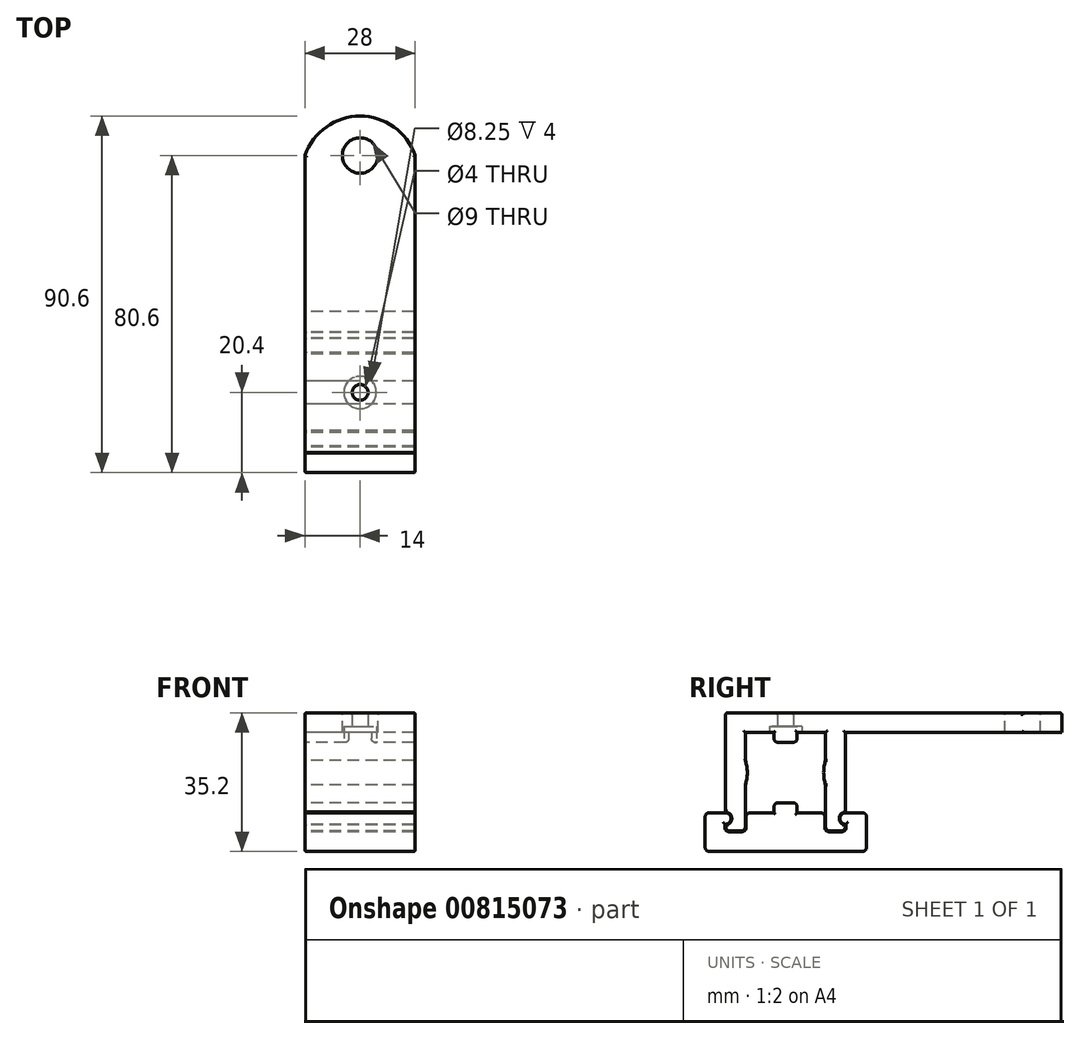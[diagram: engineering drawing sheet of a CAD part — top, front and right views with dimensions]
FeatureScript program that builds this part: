
annotation { "Feature Type Name" : "Feature", "Feature Type Description" : "" }
export const myFeature = defineFeature(function(context is Context, id is Id, definition is map)
    precondition{}
    {
        {
            var Q0;
            Q0=qCreatedBy(makeId("Right.planeOp"),FACE);
            var sketch = newSketch(context, id + "F0", { "sketchPlane" : qUnion([Q0])});
            skLineSegment(sketch, "E0.bottom", {"start": v(10, -10) * mm, "end": v(-10, -10) * mm, "construction": true});
            skLineSegment(sketch, "E0.top", {"start": v(10, 10) * mm, "end": v(-10, 10) * mm, "construction": true});
            skLineSegment(sketch, "E0.left", {"start": v(10, -10) * mm, "end": v(10, 10) * mm, "construction": true});
            skLineSegment(sketch, "E0.right", {"start": v(-10, -10) * mm, "end": v(-10, 10) * mm, "construction": true});
            skPoint(sketch, "E0.middle", {"position": v(0, 0) * mm});
            skLineSegment(sketch, "E1.bottom", {"start": v(-4, 4) * mm, "end": v(4, 4) * mm, "construction": true});
            skLineSegment(sketch, "E1.top", {"start": v(-4, -4) * mm, "end": v(4, -4) * mm, "construction": true});
            skLineSegment(sketch, "E1.left", {"start": v(-4, 4) * mm, "end": v(-4, -4) * mm, "construction": true});
            skLineSegment(sketch, "E1.right", {"start": v(4, 4) * mm, "end": v(4, -4) * mm, "construction": true});
            skLineSegment(sketch, "E2.bottom", {"start": v(3.15, -25) * mm, "end": v(-3.15, -25) * mm, "construction": true});
            skLineSegment(sketch, "E2.top", {"start": v(3.15, 25) * mm, "end": v(-3.15, 25) * mm, "construction": true});
            skLineSegment(sketch, "E2.left", {"start": v(3.15, -25) * mm, "end": v(3.15, 25) * mm, "construction": true});
            skLineSegment(sketch, "E2.right", {"start": v(-3.15, -25) * mm, "end": v(-3.15, 25) * mm, "construction": true});
            skLineSegment(sketch, "E3.bottom", {"start": v(25, -3.15) * mm, "end": v(-25, -3.15) * mm, "construction": true});
            skLineSegment(sketch, "E3.top", {"start": v(25, 3.15) * mm, "end": v(-25, 3.15) * mm, "construction": true});
            skLineSegment(sketch, "E3.left", {"start": v(25, -3.15) * mm, "end": v(25, 3.15) * mm, "construction": true});
            skLineSegment(sketch, "E3.right", {"start": v(-25, -3.15) * mm, "end": v(-25, 3.15) * mm, "construction": true});
            skSolve(sketch);
        }
        {
            assignVariable(context, id + "F1", {"name" : "ArmW", "anyValue" : 28});
        }
        {
            assignVariable(context, id + "F2", {"name" : "NobH", "anyValue" : 2.5});
        }
        {
            var Q0;
            Q0=qCreatedBy(makeId("Right.planeOp"),FACE);
            var sketch = newSketch(context, id + "F3", { "sketchPlane" : qUnion([Q0])});
            skLineSegment(sketch, "E4.bottom", {"start": v(-2.95, 10.2) * mm, "end": v(2.95, 10.2) * mm});
            skLineSegment(sketch, "E4.top", {"start": v(-1.95, 7.7) * mm, "end": v(1.95, 7.7) * mm});
            skLineSegment(sketch, "E4.left", {"start": v(-2.95, 10.2) * mm, "end": v(-2.95, 8.7) * mm});
            skLineSegment(sketch, "E4.right", {"start": v(2.95, 10.2) * mm, "end": v(2.95, 8.7) * mm});
            skLineSegment(sketch, "E5.bottom", {"start": v(-15.2, 15.2) * mm, "end": v(70.2, 15.2) * mm});
            skLineSegment(sketch, "E5.top", {"start": v(-15.2, 10.2) * mm, "end": v(15.2, 10.2) * mm});
            skLineSegment(sketch, "E5.left", {"start": v(-15.2, 15.2) * mm, "end": v(-15.2, 10.2) * mm});
            skLineSegment(sketch, "E5.right", {"start": v(70.2, 15.2) * mm, "end": v(70.2, 10.2) * mm});
            skLineSegment(sketch, "E6.bottom", {"start": v(10.2, 10.2) * mm, "end": v(15.2, 10.2) * mm});
            skLineSegment(sketch, "E6.top", {"start": v(11.2, -14.8) * mm, "end": v(14.2, -14.8) * mm});
            skLineSegment(sketch, "E6.left", {"start": v(10.2, 10.2) * mm, "end": v(10.2, -13.8) * mm});
            skLineSegment(sketch, "E6.right", {"start": v(15.2, -10) * mm, "end": v(15.2, -10.09) * mm});
            skLineSegment(sketch, "E7.bottom", {"start": v(-15.2, 10.2) * mm, "end": v(-10.2, 10.2) * mm});
            skLineSegment(sketch, "E7.top", {"start": v(-14.2, -14.8) * mm, "end": v(-11.2, -14.8) * mm});
            skLineSegment(sketch, "E7.left", {"start": v(-15.2, 10.2) * mm, "end": v(-15.2, -10) * mm});
            skLineSegment(sketch, "E7.right", {"start": v(-10.2, 10.2) * mm, "end": v(-10.2, -13.8) * mm});
            skLineSegment(sketch, "E8.bottom", {"start": v(9.7, -1.7) * mm, "end": v(-9.7, -1.7) * mm, "construction": true});
            skLineSegment(sketch, "E8.top", {"start": v(9.7, 1.7) * mm, "end": v(-9.7, 1.7) * mm, "construction": true});
            skLineSegment(sketch, "E8.left", {"start": v(9.7, -1.7) * mm, "end": v(9.7, 1.7) * mm, "construction": true});
            skLineSegment(sketch, "E8.right", {"start": v(-9.7, -1.7) * mm, "end": v(-9.7, 1.7) * mm, "construction": true});
            skPoint(sketch, "E8.middle", {"position": v(0, 0) * mm});
            skPoint(sketch, "E9", {"position": v(-10.2, 3.15) * mm});
            skPoint(sketch, "E10", {"position": v(-10.2, -3.15) * mm});
            skPoint(sketch, "E11", {"position": v(-9.7, 0) * mm});
            skPoint(sketch, "E12", {"position": v(10.2, 3.15) * mm});
            skPoint(sketch, "E13", {"position": v(10.2, -3.15) * mm});
            skPoint(sketch, "E14", {"position": v(9.7, 0) * mm});
            skArc(sketch, "E15", {"start": v(-10.2, -3.15) * mm, "mid": v(-9.7, 0) * mm, "end": v(-10.2, 3.15) * mm});
            skArc(sketch, "E16", {"start": v(10.2, 3.15) * mm, "mid": v(9.7, 0) * mm, "end": v(10.2, -3.15) * mm});
            skLineSegment(sketch, "E17.bottom", {"start": v(-9, -10.2) * mm, "end": v(9, -10.2) * mm});
            skLineSegment(sketch, "E17.left", {"start": v(-10, -11.2) * mm, "end": v(-10, -14) * mm});
            skLineSegment(sketch, "E17.right", {"start": v(10, -11.2) * mm, "end": v(10, -14) * mm});
            skLineSegment(sketch, "E18.bottom", {"start": v(-19.4, -10.2) * mm, "end": v(-15.4, -10.2) * mm});
            skLineSegment(sketch, "E18.top", {"start": v(-19.4, -20) * mm, "end": v(-15.4, -20) * mm});
            skLineSegment(sketch, "E18.left", {"start": v(-20.4, -11.2) * mm, "end": v(-20.4, -19) * mm});
            skLineSegment(sketch, "E18.right", {"start": v(-15.4, -13.1) * mm, "end": v(-15.4, -14) * mm});
            skLineSegment(sketch, "E19.bottom", {"start": v(15.4, -10.2) * mm, "end": v(19.6, -10.2) * mm});
            skLineSegment(sketch, "E19.top", {"start": v(15.6, -20) * mm, "end": v(19.6, -20) * mm});
            skLineSegment(sketch, "E19.left", {"start": v(15.4, -13.1) * mm, "end": v(15.4, -14) * mm});
            skLineSegment(sketch, "E19.right", {"start": v(20.6, -11.2) * mm, "end": v(20.6, -19) * mm});
            skLineSegment(sketch, "E20.bottom", {"start": v(-14.4, -15) * mm, "end": v(-11, -15) * mm});
            skLineSegment(sketch, "E20.top", {"start": v(-15.4, -20) * mm, "end": v(15.6, -20) * mm});
            skLineSegment(sketch, "E20.left", {"start": v(-15.4, -15) * mm, "end": v(-15.4, -20) * mm});
            skLineSegment(sketch, "E20.right", {"start": v(15.6, -20) * mm, "end": v(15.6, -20) * mm});
            skLineSegment(sketch, "E21.bottom", {"start": v(-1.95, -7.7) * mm, "end": v(1.95, -7.7) * mm});
            skLineSegment(sketch, "E21.top", {"start": v(-2.95, -10.2) * mm, "end": v(2.95, -10.2) * mm});
            skLineSegment(sketch, "E21.left", {"start": v(-2.95, -8.7) * mm, "end": v(-2.95, -10.2) * mm});
            skLineSegment(sketch, "E21.right", {"start": v(2.95, -8.7) * mm, "end": v(2.95, -10.2) * mm});
            skPoint(sketch, "E22", {"position": v(-15.2, -10) * mm});
            skPoint(sketch, "E23", {"position": v(-15.2, -13.3) * mm});
            skPoint(sketch, "E24", {"position": v(-15.4, -13.1) * mm});
            skPoint(sketch, "E25", {"position": v(-13.65, -11.8) * mm});
            skPoint(sketch, "E26", {"position": v(-13.85, -11.8) * mm});
            skArc(sketch, "E27", {"start": v(-15.2, -13.3) * mm, "mid": v(-13.64, -11.65) * mm, "end": v(-15.2, -10) * mm});
            skArc(sketch, "E28", {"start": v(-15.4, -13.1) * mm, "mid": v(-13.84, -11.65) * mm, "end": v(-15.4, -10.2) * mm});
            skLineSegment(sketch, "E29.trimOffspring", {"start": v(-15.2, -13.3) * mm, "end": v(-15.2, -13.8) * mm});
            skPoint(sketch, "E30.MirrorP", {"position": v(15.2, -10) * mm});
            skArc(sketch, "E31.MirrorCS", {"start": v(15.2, -13.3) * mm, "mid": v(13.64, -11.65) * mm, "end": v(15.2, -10) * mm});
            skArc(sketch, "E32.MirrorCS", {"start": v(15.4, -13.1) * mm, "mid": v(13.84, -11.65) * mm, "end": v(15.4, -10.2) * mm});
            skPoint(sketch, "E33.MirrorP", {"position": v(13.85, -11.8) * mm});
            skPoint(sketch, "E34.MirrorP", {"position": v(13.65, -11.8) * mm});
            skPoint(sketch, "E35.MirrorP", {"position": v(15.4, -13.1) * mm});
            skPoint(sketch, "E36.MirrorP", {"position": v(15.2, -13.3) * mm});
            skLineSegment(sketch, "E37.trimOffspring", {"start": v(15.2, -13.3) * mm, "end": v(15.2, -13.8) * mm});
            skPoint(sketch, "E38.visualSharp", {"position": v(-15.2, 15.2) * mm});
            skPoint(sketch, "E39.visualSharp", {"position": v(-20.4, -10.2) * mm});
            skArc(sketch, "E39.filletArc", {"start": v(-19.4, -10.2) * mm, "mid": v(-20.1, -10.5) * mm, "end": v(-20.4, -11.2) * mm});
            skPoint(sketch, "E40.visualSharp", {"position": v(-20.4, -20) * mm});
            skArc(sketch, "E40.filletArc", {"start": v(-20.4, -19) * mm, "mid": v(-20.1, -19.7) * mm, "end": v(-19.4, -20) * mm});
            skPoint(sketch, "E41.visualSharp", {"position": v(20.6, -20) * mm});
            skArc(sketch, "E41.filletArc", {"start": v(19.6, -20) * mm, "mid": v(20.3, -19.7) * mm, "end": v(20.6, -19) * mm});
            skPoint(sketch, "E42.visualSharp", {"position": v(20.6, -10.2) * mm});
            skArc(sketch, "E42.filletArc", {"start": v(20.6, -11.2) * mm, "mid": v(20.3, -10.5) * mm, "end": v(19.6, -10.2) * mm});
            skPoint(sketch, "E43.visualSharp", {"position": v(-2.95, -7.7) * mm});
            skArc(sketch, "E43.filletArc", {"start": v(-1.95, -7.7) * mm, "mid": v(-2.66, -8) * mm, "end": v(-2.95, -8.7) * mm});
            skPoint(sketch, "E44.visualSharp", {"position": v(2.95, -7.7) * mm});
            skArc(sketch, "E44.filletArc", {"start": v(2.95, -8.7) * mm, "mid": v(2.66, -8) * mm, "end": v(1.95, -7.7) * mm});
            skPoint(sketch, "E45.visualSharp", {"position": v(-2.95, 7.7) * mm});
            skArc(sketch, "E45.filletArc", {"start": v(-2.95, 8.7) * mm, "mid": v(-2.66, 8) * mm, "end": v(-1.95, 7.7) * mm});
            skPoint(sketch, "E46.visualSharp", {"position": v(2.95, 7.7) * mm});
            skArc(sketch, "E46.filletArc", {"start": v(1.95, 7.7) * mm, "mid": v(2.66, 8) * mm, "end": v(2.95, 8.7) * mm});
            skPoint(sketch, "E47.visualSharp", {"position": v(10.2, -14.8) * mm});
            skArc(sketch, "E47.filletArc", {"start": v(10.2, -13.8) * mm, "mid": v(10.5, -14.5) * mm, "end": v(11.2, -14.8) * mm});
            skPoint(sketch, "E48.visualSharp", {"position": v(15.2, -14.8) * mm});
            skArc(sketch, "E48.filletArc", {"start": v(14.2, -14.8) * mm, "mid": v(14.9, -14.5) * mm, "end": v(15.2, -13.8) * mm});
            skPoint(sketch, "E49.visualSharp", {"position": v(-10, -10.2) * mm});
            skArc(sketch, "E49.filletArc", {"start": v(-9, -10.2) * mm, "mid": v(-9.7, -10.5) * mm, "end": v(-10, -11.2) * mm});
            skPoint(sketch, "E50.visualSharp", {"position": v(10, -10.2) * mm});
            skArc(sketch, "E50.filletArc", {"start": v(10, -11.2) * mm, "mid": v(9.7, -10.5) * mm, "end": v(9, -10.2) * mm});
            skPoint(sketch, "E51.visualSharp", {"position": v(-10.2, -14.8) * mm});
            skArc(sketch, "E51.filletArc", {"start": v(-11.2, -14.8) * mm, "mid": v(-10.5, -14.5) * mm, "end": v(-10.2, -13.8) * mm});
            skPoint(sketch, "E52.visualSharp", {"position": v(-15.2, -14.8) * mm});
            skArc(sketch, "E52.filletArc", {"start": v(-15.2, -13.8) * mm, "mid": v(-14.9, -14.5) * mm, "end": v(-14.2, -14.8) * mm});
            skArc(sketch, "E53.filletArc", {"start": v(-15.4, -14) * mm, "mid": v(-15.1, -14.7) * mm, "end": v(-14.4, -15) * mm});
            skArc(sketch, "E54.filletArc", {"start": v(14.4, -15) * mm, "mid": v(15.1, -14.7) * mm, "end": v(15.4, -14) * mm});
            skLineSegment(sketch, "E55.trimOffspring", {"start": v(11, -15) * mm, "end": v(14.4, -15) * mm});
            skPoint(sketch, "E56.visualSharp", {"position": v(-10, -15) * mm});
            skArc(sketch, "E56.filletArc", {"start": v(-11, -15) * mm, "mid": v(-10.3, -14.7) * mm, "end": v(-10, -14) * mm});
            skPoint(sketch, "E57.visualSharp", {"position": v(10, -15) * mm});
            skArc(sketch, "E57.filletArc", {"start": v(10, -14) * mm, "mid": v(10.3, -14.7) * mm, "end": v(11, -15) * mm});
            skPoint(sketch, "E58.visualSharp", {"position": v(-15.4, -10.2) * mm});
            skLineSegment(sketch, "E59", {"start": v(15.2, 10.2) * mm, "end": v(15.2, -10.09) * mm});
            skLineSegment(sketch, "E60", {"start": v(15.2, 10.2) * mm, "end": v(70.2, 10.2) * mm});
            skSolve(sketch);
        }
        {
            var Q0;
            Q0=qSketchRegion(id+"F3",true);
            extrude(context, id + "F4", {"entities" : qUnion([Q0]), "depth" : (getVariable(context, 'ArmW')) * mm, "offsetDistance" : 25 * mm});
        }
        {
            var Q0;
            Q0=makeQuery(id+"F4.opExtrude","SWEPT_FACE",FACE,{"disambiguationData":[OSD([sQuery(id+"F3.wireOp",EDGE,"E4.top")])]});
            cPlane(context, id + "F5", {"entities" : qUnion([Q0]), "cplaneType" : CPlaneType.OFFSET, "offset" : 0 * mm, "width" : 150 * mm, "height" : 150 * mm});
        }
        {
            var Q0;
            Q0=qCreatedBy(id+"F5.planeOp",FACE);
            var sketch = newSketch(context, id + "F6", { "sketchPlane" : qUnion([Q0])});
            skLineSegment(sketch, "E61", {"start": v(28, -15.2) * mm, "end": v(0, 15.2) * mm, "construction": true});
            skLineSegment(sketch, "E62", {"start": v(28, 15.2) * mm, "end": v(0, -15.2) * mm, "construction": true});
            skPoint(sketch, "E63", {"position": v(14, 0) * mm});
            skPoint(sketch, "E64.0", {"position": v(28, -15.2) * mm});
            skLineSegment(sketch, "E65.bottom", {"start": v(0, -15.2) * mm, "end": v(2, -15.2) * mm, "construction": true});
            skLineSegment(sketch, "E65.top", {"start": v(0, -13.2) * mm, "end": v(2, -13.2) * mm, "construction": true});
            skLineSegment(sketch, "E65.left", {"start": v(0, -15.2) * mm, "end": v(0, -13.2) * mm, "construction": true});
            skLineSegment(sketch, "E65.right", {"start": v(2, -15.2) * mm, "end": v(2, -13.2) * mm, "construction": true});
            skLineSegment(sketch, "E66.bottom", {"start": v(26, -13.2) * mm, "end": v(28, -13.2) * mm, "construction": true});
            skLineSegment(sketch, "E66.top", {"start": v(26, -15.2) * mm, "end": v(28, -15.2) * mm, "construction": true});
            skLineSegment(sketch, "E66.left", {"start": v(26, -13.2) * mm, "end": v(26, -15.2) * mm, "construction": true});
            skLineSegment(sketch, "E66.right", {"start": v(28, -13.2) * mm, "end": v(28, -15.2) * mm, "construction": true});
            skLineSegment(sketch, "E67.bottom", {"start": v(26, 15.2) * mm, "end": v(28, 15.2) * mm, "construction": true});
            skLineSegment(sketch, "E67.top", {"start": v(26, 13.2) * mm, "end": v(28, 13.2) * mm, "construction": true});
            skLineSegment(sketch, "E67.left", {"start": v(26, 15.2) * mm, "end": v(26, 13.2) * mm, "construction": true});
            skLineSegment(sketch, "E67.right", {"start": v(28, 15.2) * mm, "end": v(28, 13.2) * mm, "construction": true});
            skLineSegment(sketch, "E68.bottom", {"start": v(0, 15.2) * mm, "end": v(2, 15.2) * mm, "construction": true});
            skLineSegment(sketch, "E68.top", {"start": v(0, 13.2) * mm, "end": v(2, 13.2) * mm, "construction": true});
            skLineSegment(sketch, "E68.left", {"start": v(0, 15.2) * mm, "end": v(0, 13.2) * mm, "construction": true});
            skLineSegment(sketch, "E68.right", {"start": v(2, 15.2) * mm, "end": v(2, 13.2) * mm, "construction": true});
            skSolve(sketch);
        }
        {
            var Q0;
            Q0=sQuery(id+"F6.wireOp",VERTEX,"E63");
            var Q1;
            Q1=makeQuery(id+"F4.opExtrude","SWEPT_BODY",BODY,{"disambiguationData":[OSD([sQuery(id+"F3.wireOp",EDGE,"E4.top"),sQuery(id+"F3.wireOp",EDGE,"E4.left"),sQuery(id+"F3.wireOp",EDGE,"E4.right"),sQuery(id+"F3.wireOp",EDGE,"E5.bottom"),sQuery(id+"F3.wireOp",EDGE,"E5.top"),sQuery(id+"F3.wireOp",EDGE,"E5.left"),sQuery(id+"F3.wireOp",EDGE,"E5.right"),sQuery(id+"F3.wireOp",EDGE,"E6.top"),sQuery(id+"F3.wireOp",EDGE,"E6.left"),sQuery(id+"F3.wireOp",EDGE,"E6.right"),sQuery(id+"F3.wireOp",EDGE,"E7.top"),sQuery(id+"F3.wireOp",EDGE,"E7.left"),sQuery(id+"F3.wireOp",EDGE,"E7.right"),sQuery(id+"F3.wireOp",EDGE,"E15"),sQuery(id+"F3.wireOp",EDGE,"E16"),sQuery(id+"F3.wireOp",EDGE,"E27"),sQuery(id+"F3.wireOp",EDGE,"E29.trimOffspring"),sQuery(id+"F3.wireOp",EDGE,"E31.MirrorCS"),sQuery(id+"F3.wireOp",EDGE,"E37.trimOffspring"),sQuery(id+"F3.wireOp",EDGE,"E45.filletArc"),sQuery(id+"F3.wireOp",EDGE,"E46.filletArc"),sQuery(id+"F3.wireOp",EDGE,"E47.filletArc"),sQuery(id+"F3.wireOp",EDGE,"E48.filletArc"),sQuery(id+"F3.wireOp",EDGE,"E51.filletArc"),sQuery(id+"F3.wireOp",EDGE,"E52.filletArc"),sQuery(id+"F3.wireOp",EDGE,"E59")])]});
            hole(context, id + "F7", {"style" : HoleStyle.C_BORE, "endStyle" : HoleEndStyle.THROUGH, "holeDiameter" : 4 * mm, "cBoreDiameter" : 8.25 * mm, "cBoreDepth" : (getVariable(context, 'NobH') + 1.5) * mm, "majorDiameter" : 3 * mm, "isTappedThrough" : true, "tappedDepth" : 6.5 * mm, "tapClearance" : 3, "startFromSketch" : true, "locations" : qUnion([Q0]), "scope" : qUnion([Q1])});
        }
        {
            var Q0;
            Q0=makeQuery(id+"F4.opExtrude","SWEPT_FACE",FACE,{"disambiguationData":[OSD([sQuery(id+"F3.wireOp",EDGE,"E5.bottom")])]});
            var sketch = newSketch(context, id + "F8", { "sketchPlane" : qUnion([Q0])});
            skPoint(sketch, "E69.0", {"position": v(28, 15.2) * mm});
            skPoint(sketch, "E70.0", {"position": v(0, 15.2) * mm});
            skLineSegment(sketch, "E71.bottom", {"start": v(0, 15.2) * mm, "end": v(28, 15.2) * mm, "construction": true});
            skLineSegment(sketch, "E71.top", {"start": v(0, 60.2) * mm, "end": v(28, 60.2) * mm, "construction": true});
            skLineSegment(sketch, "E71.left", {"start": v(0, 15.2) * mm, "end": v(0, 60.2) * mm, "construction": true});
            skLineSegment(sketch, "E71.right", {"start": v(28, 15.2) * mm, "end": v(28, 60.2) * mm, "construction": true});
            skPoint(sketch, "E72", {"position": v(14, 60.2) * mm});
            skArc(sketch, "E73", {"start": v(28, 60.2) * mm, "mid": v(14, 70.2) * mm, "end": v(0, 60.2) * mm});
            skSolve(sketch);
        }
        {
            var Q0;
            Q0=sQuery(id+"F8.wireOp",VERTEX,"E72");
            var Q1;
            Q1=makeQuery(id+"F4.opExtrude","SWEPT_BODY",BODY,{"disambiguationData":[OSD([sQuery(id+"F3.wireOp",EDGE,"E4.top"),sQuery(id+"F3.wireOp",EDGE,"E4.left"),sQuery(id+"F3.wireOp",EDGE,"E4.right"),sQuery(id+"F3.wireOp",EDGE,"E5.bottom"),sQuery(id+"F3.wireOp",EDGE,"E5.top"),sQuery(id+"F3.wireOp",EDGE,"E5.left"),sQuery(id+"F3.wireOp",EDGE,"E5.right"),sQuery(id+"F3.wireOp",EDGE,"E6.top"),sQuery(id+"F3.wireOp",EDGE,"E6.left"),sQuery(id+"F3.wireOp",EDGE,"E7.top"),sQuery(id+"F3.wireOp",EDGE,"E7.left"),sQuery(id+"F3.wireOp",EDGE,"E7.right"),sQuery(id+"F3.wireOp",EDGE,"E15"),sQuery(id+"F3.wireOp",EDGE,"E16"),sQuery(id+"F3.wireOp",EDGE,"E27"),sQuery(id+"F3.wireOp",EDGE,"E29.trimOffspring"),sQuery(id+"F3.wireOp",EDGE,"E31.MirrorCS"),sQuery(id+"F3.wireOp",EDGE,"E37.trimOffspring"),sQuery(id+"F3.wireOp",EDGE,"E45.filletArc"),sQuery(id+"F3.wireOp",EDGE,"E46.filletArc"),sQuery(id+"F3.wireOp",EDGE,"E47.filletArc"),sQuery(id+"F3.wireOp",EDGE,"E48.filletArc"),sQuery(id+"F3.wireOp",EDGE,"E51.filletArc"),sQuery(id+"F3.wireOp",EDGE,"E52.filletArc"),sQuery(id+"F3.wireOp",EDGE,"E59"),sQuery(id+"F3.wireOp",EDGE,"E60")])]});
            hole(context, id + "F9", {"style" : HoleStyle.SIMPLE, "endStyle" : HoleEndStyle.THROUGH, "holeDiameter" : 9 * mm, "majorDiameter" : 5 * mm, "isTappedThrough" : true, "tappedDepth" : 6.5 * mm, "tapClearance" : 3, "startFromSketch" : true, "locations" : qUnion([Q0]), "scope" : qUnion([Q1])});
        }
        {
            var Q0;
            {var subQ0=sQuery(id+"F8.wireOp",EDGE,"E73");var subQ1=sQuery(id+"F3.wireOp",EDGE,"E5.bottom");var subQ2=makeQuery(id+"F4.opExtrude","SWEPT_FACE",FACE,{"disambiguationData":[OSD([subQ1])]});var subQ3=makeQuery(id+"F11.opFillet","BLEND_EDGE",EDGE,{"blendedFrom":[makeQuery(id+"F4.opExtrude","CAP_EDGE",EDGE,{"disambiguationData":[OSD([subQ1])],"isStart":true}),subQ2],"blendedInto":[subQ2]});var subQ4=makeQuery(id+"F8.imprint","INTERSECT",VERTEX,{"derivedFrom":[subQ3,subQ0]});Q0=makeQuery(id+"F8.imprint","IMPRINT",FACE,{"disambiguationData":[TD([[makeQuery(id+"F8.imprint","IMPRINT",EDGE,{"disambiguationData":[TD([[subQ4,1.0]])],"derivedFrom":subQ0}),-1.0]])]});}
            var Q1;
            {var subQ0=sQuery(id+"F8.wireOp",EDGE,"E73");var subQ1=sQuery(id+"F3.wireOp",EDGE,"E5.bottom");var subQ2=makeQuery(id+"F4.opExtrude","SWEPT_FACE",FACE,{"disambiguationData":[OSD([subQ1])]});var subQ3=makeQuery(id+"F11.opFillet","BLEND_EDGE",EDGE,{"blendedFrom":[makeQuery(id+"F4.opExtrude","CAP_EDGE",EDGE,{"disambiguationData":[OSD([subQ1])],"isStart":false}),subQ2],"blendedInto":[subQ2]});var subQ4=makeQuery(id+"F8.imprint","INTERSECT",VERTEX,{"derivedFrom":[subQ3,subQ0]});Q1=makeQuery(id+"F8.imprint","IMPRINT",FACE,{"disambiguationData":[TD([[makeQuery(id+"F8.imprint","IMPRINT",EDGE,{"disambiguationData":[TD([[subQ4,-1.0]])],"derivedFrom":subQ0}),-1.0]])]});}
            extrude(context, id + "F10", {"entities" : qUnion([Q0, Q1]), "operationType" : NewBodyOperationType.REMOVE, "endBound" : BoundingType.UP_TO_NEXT, "oppositeDirection" : true, "depth" : 25 * mm, "offsetDistance" : 25 * mm});
        }
        {
            var Q0;
            Q0=makeQuery(id+"F4.opExtrude","CAP_FACE",FACE,{"disambiguationData":[OSD([sQuery(id+"F3.wireOp",EDGE,"E4.top"),sQuery(id+"F3.wireOp",EDGE,"E4.left"),sQuery(id+"F3.wireOp",EDGE,"E4.right"),sQuery(id+"F3.wireOp",EDGE,"E5.bottom"),sQuery(id+"F3.wireOp",EDGE,"E5.top"),sQuery(id+"F3.wireOp",EDGE,"E5.left"),sQuery(id+"F3.wireOp",EDGE,"E5.right"),sQuery(id+"F3.wireOp",EDGE,"E6.top"),sQuery(id+"F3.wireOp",EDGE,"E6.left"),sQuery(id+"F3.wireOp",EDGE,"E7.top"),sQuery(id+"F3.wireOp",EDGE,"E7.left"),sQuery(id+"F3.wireOp",EDGE,"E7.right"),sQuery(id+"F3.wireOp",EDGE,"E15"),sQuery(id+"F3.wireOp",EDGE,"E16"),sQuery(id+"F3.wireOp",EDGE,"E27"),sQuery(id+"F3.wireOp",EDGE,"E29.trimOffspring"),sQuery(id+"F3.wireOp",EDGE,"E31.MirrorCS"),sQuery(id+"F3.wireOp",EDGE,"E37.trimOffspring"),sQuery(id+"F3.wireOp",EDGE,"E45.filletArc"),sQuery(id+"F3.wireOp",EDGE,"E46.filletArc"),sQuery(id+"F3.wireOp",EDGE,"E47.filletArc"),sQuery(id+"F3.wireOp",EDGE,"E48.filletArc"),sQuery(id+"F3.wireOp",EDGE,"E51.filletArc"),sQuery(id+"F3.wireOp",EDGE,"E52.filletArc"),sQuery(id+"F3.wireOp",EDGE,"E59"),sQuery(id+"F3.wireOp",EDGE,"E60")])],"isStart":true});
            var Q1;
            Q1=makeQuery(id+"F4.opExtrude","CAP_FACE",FACE,{"disambiguationData":[OSD([sQuery(id+"F3.wireOp",EDGE,"E4.top"),sQuery(id+"F3.wireOp",EDGE,"E4.left"),sQuery(id+"F3.wireOp",EDGE,"E4.right"),sQuery(id+"F3.wireOp",EDGE,"E5.bottom"),sQuery(id+"F3.wireOp",EDGE,"E5.top"),sQuery(id+"F3.wireOp",EDGE,"E5.left"),sQuery(id+"F3.wireOp",EDGE,"E5.right"),sQuery(id+"F3.wireOp",EDGE,"E6.top"),sQuery(id+"F3.wireOp",EDGE,"E6.left"),sQuery(id+"F3.wireOp",EDGE,"E7.top"),sQuery(id+"F3.wireOp",EDGE,"E7.left"),sQuery(id+"F3.wireOp",EDGE,"E7.right"),sQuery(id+"F3.wireOp",EDGE,"E15"),sQuery(id+"F3.wireOp",EDGE,"E16"),sQuery(id+"F3.wireOp",EDGE,"E27"),sQuery(id+"F3.wireOp",EDGE,"E29.trimOffspring"),sQuery(id+"F3.wireOp",EDGE,"E31.MirrorCS"),sQuery(id+"F3.wireOp",EDGE,"E37.trimOffspring"),sQuery(id+"F3.wireOp",EDGE,"E45.filletArc"),sQuery(id+"F3.wireOp",EDGE,"E46.filletArc"),sQuery(id+"F3.wireOp",EDGE,"E47.filletArc"),sQuery(id+"F3.wireOp",EDGE,"E48.filletArc"),sQuery(id+"F3.wireOp",EDGE,"E51.filletArc"),sQuery(id+"F3.wireOp",EDGE,"E52.filletArc"),sQuery(id+"F3.wireOp",EDGE,"E59"),sQuery(id+"F3.wireOp",EDGE,"E60")])],"isStart":false});
            fillet(context, id + "F11", {"entities" : qUnion([Q0, Q1]), "radius" : .4 * mm, "tangentPropagation" : true, "allowEdgeOverflow" : false});
        }
        {
            var Q0;
            Q0=makeQuery(id+"F4.opExtrude","CAP_FACE",FACE,{"disambiguationData":[OSD([sQuery(id+"F3.wireOp",EDGE,"E17.bottom"),sQuery(id+"F3.wireOp",EDGE,"E17.left"),sQuery(id+"F3.wireOp",EDGE,"E17.right"),sQuery(id+"F3.wireOp",EDGE,"E18.bottom"),sQuery(id+"F3.wireOp",EDGE,"E18.top"),sQuery(id+"F3.wireOp",EDGE,"E18.left"),sQuery(id+"F3.wireOp",EDGE,"E18.right"),sQuery(id+"F3.wireOp",EDGE,"E19.bottom"),sQuery(id+"F3.wireOp",EDGE,"E19.top"),sQuery(id+"F3.wireOp",EDGE,"E19.left"),sQuery(id+"F3.wireOp",EDGE,"E19.right"),sQuery(id+"F3.wireOp",EDGE,"E20.bottom"),sQuery(id+"F3.wireOp",EDGE,"E20.top"),sQuery(id+"F3.wireOp",EDGE,"E21.bottom"),sQuery(id+"F3.wireOp",EDGE,"E21.left"),sQuery(id+"F3.wireOp",EDGE,"E21.right"),sQuery(id+"F3.wireOp",EDGE,"E28"),sQuery(id+"F3.wireOp",EDGE,"E32.MirrorCS")])],"isStart":false});
            var Q1;
            Q1=makeQuery(id+"F4.opExtrude","CAP_FACE",FACE,{"disambiguationData":[OSD([sQuery(id+"F3.wireOp",EDGE,"E17.bottom"),sQuery(id+"F3.wireOp",EDGE,"E17.left"),sQuery(id+"F3.wireOp",EDGE,"E17.right"),sQuery(id+"F3.wireOp",EDGE,"E18.bottom"),sQuery(id+"F3.wireOp",EDGE,"E18.top"),sQuery(id+"F3.wireOp",EDGE,"E18.left"),sQuery(id+"F3.wireOp",EDGE,"E18.right"),sQuery(id+"F3.wireOp",EDGE,"E19.bottom"),sQuery(id+"F3.wireOp",EDGE,"E19.top"),sQuery(id+"F3.wireOp",EDGE,"E19.left"),sQuery(id+"F3.wireOp",EDGE,"E19.right"),sQuery(id+"F3.wireOp",EDGE,"E20.bottom"),sQuery(id+"F3.wireOp",EDGE,"E20.top"),sQuery(id+"F3.wireOp",EDGE,"E21.bottom"),sQuery(id+"F3.wireOp",EDGE,"E21.left"),sQuery(id+"F3.wireOp",EDGE,"E21.right"),sQuery(id+"F3.wireOp",EDGE,"E28"),sQuery(id+"F3.wireOp",EDGE,"E32.MirrorCS")])],"isStart":true});
            fillet(context, id + "F12", {"entities" : qUnion([Q0, Q1]), "radius" : .4 * mm, "allowEdgeOverflow" : false});
        }
        {
            var Q0;
            Q0=makeQuery(id+"F4.opExtrude","SWEPT_FACE",FACE,{"disambiguationData":[OSD([sQuery(id+"F3.wireOp",EDGE,"E5.bottom")])]});
            var Q1;
            {var subQ0=sQuery(id+"F3.wireOp",EDGE,"E5.top");Q1=makeQuery(id+"F7.hole-0.boolean.opBoolean","INTERSECT",EDGE,{"derivedFrom":[makeQuery(id+"F4.opExtrude","SWEPT_FACE",FACE,{"disambiguationData":[OSD([subQ0]),TDD([makeQuery(id+"F3.imprint","IMPRINT",EDGE,{"disambiguationData":[TD([[makeQuery(id+"F3.imprint","INTERSECT",VERTEX,{"derivedFrom":[sQuery(id+"F3.wireOp",EDGE,"E4.right"),subQ0]}),-1.0]])],"derivedFrom":subQ0})])]}),makeQuery(id+"F7.hole-0.opRevolve","SWEPT_FACE",FACE,{"disambiguationData":[OSD([sQuery(id+"F7.hole-0.sketch.wireOp",EDGE,"cbore_start_line_2")])]})]});}
            var Q2;
            {var subQ0=sQuery(id+"F3.wireOp",EDGE,"E5.top");Q2=makeQuery(id+"F7.hole-0.boolean.opBoolean","INTERSECT",EDGE,{"derivedFrom":[makeQuery(id+"F4.opExtrude","SWEPT_FACE",FACE,{"disambiguationData":[OSD([subQ0]),TDD([makeQuery(id+"F3.imprint","IMPRINT",EDGE,{"disambiguationData":[TD([[makeQuery(id+"F3.imprint","INTERSECT",VERTEX,{"derivedFrom":[sQuery(id+"F3.wireOp",EDGE,"E4.left"),subQ0]}),1.0]])],"derivedFrom":subQ0})])]}),makeQuery(id+"F7.hole-0.opRevolve","SWEPT_FACE",FACE,{"disambiguationData":[OSD([sQuery(id+"F7.hole-0.sketch.wireOp",EDGE,"cbore_start_line_2")])]})]});}
            var Q3;
            Q3=makeQuery(id+"F7.hole-0.boolean.opBoolean","COPY",FACE,{"derivedFrom":makeQuery(id+"F7.hole-0.opRevolve","SWEPT_FACE",FACE,{"disambiguationData":[OSD([sQuery(id+"F7.hole-0.sketch.wireOp",EDGE,"cbore_start_line_2")])]})});
            var Q4;
            Q4=makeQuery(id+"F9.hole-0.boolean.opBoolean","INTERSECT",EDGE,{"derivedFrom":[makeQuery(id+"F4.opExtrude","SWEPT_FACE",FACE,{"disambiguationData":[OSD([sQuery(id+"F3.wireOp",EDGE,"E60")])]}),makeQuery(id+"F9.hole-0.opRevolve","SWEPT_FACE",FACE,{"disambiguationData":[OSD([sQuery(id+"F9.hole-0.sketch.wireOp",EDGE,"core_line_2")])]})]});
            fillet(context, id + "F13", {"entities" : qUnion([Q0, Q1, Q2, Q3, Q4]), "radius" : .5 * mm, "tangentPropagation" : true, "allowEdgeOverflow" : false});
        }
    });
